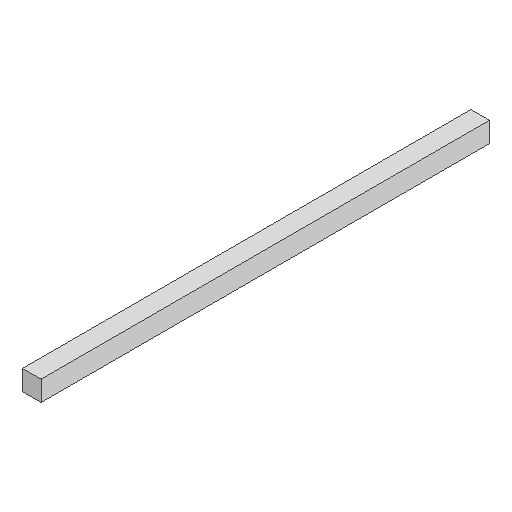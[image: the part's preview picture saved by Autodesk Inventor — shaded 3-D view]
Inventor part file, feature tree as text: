
AUTODESK INVENTOR PART (.ipt)
format: ipt  version: 2024 (Build 280153000, 153)  size: 80,896 bytes
history: native  units: in
note: dims shown in document units (in); Inventor stores cm internally (conversion verified against a paired STEP export)
features: extrude x1, sketch x1
ambient origin geometry x8: Origin, YZ Plane, XZ Plane, XY Plane, X Axis, Y Axis, Z Axis, Center Point
bodies: Solid1 (feature_tree)
feature tree (2):
  extrude  "Extrusion1"  Depth=7.0866in
  sketch  "Sketch1"  dims[d0=6.5354in d1=7.0866in d2=157.4803in d3=0.0in]
